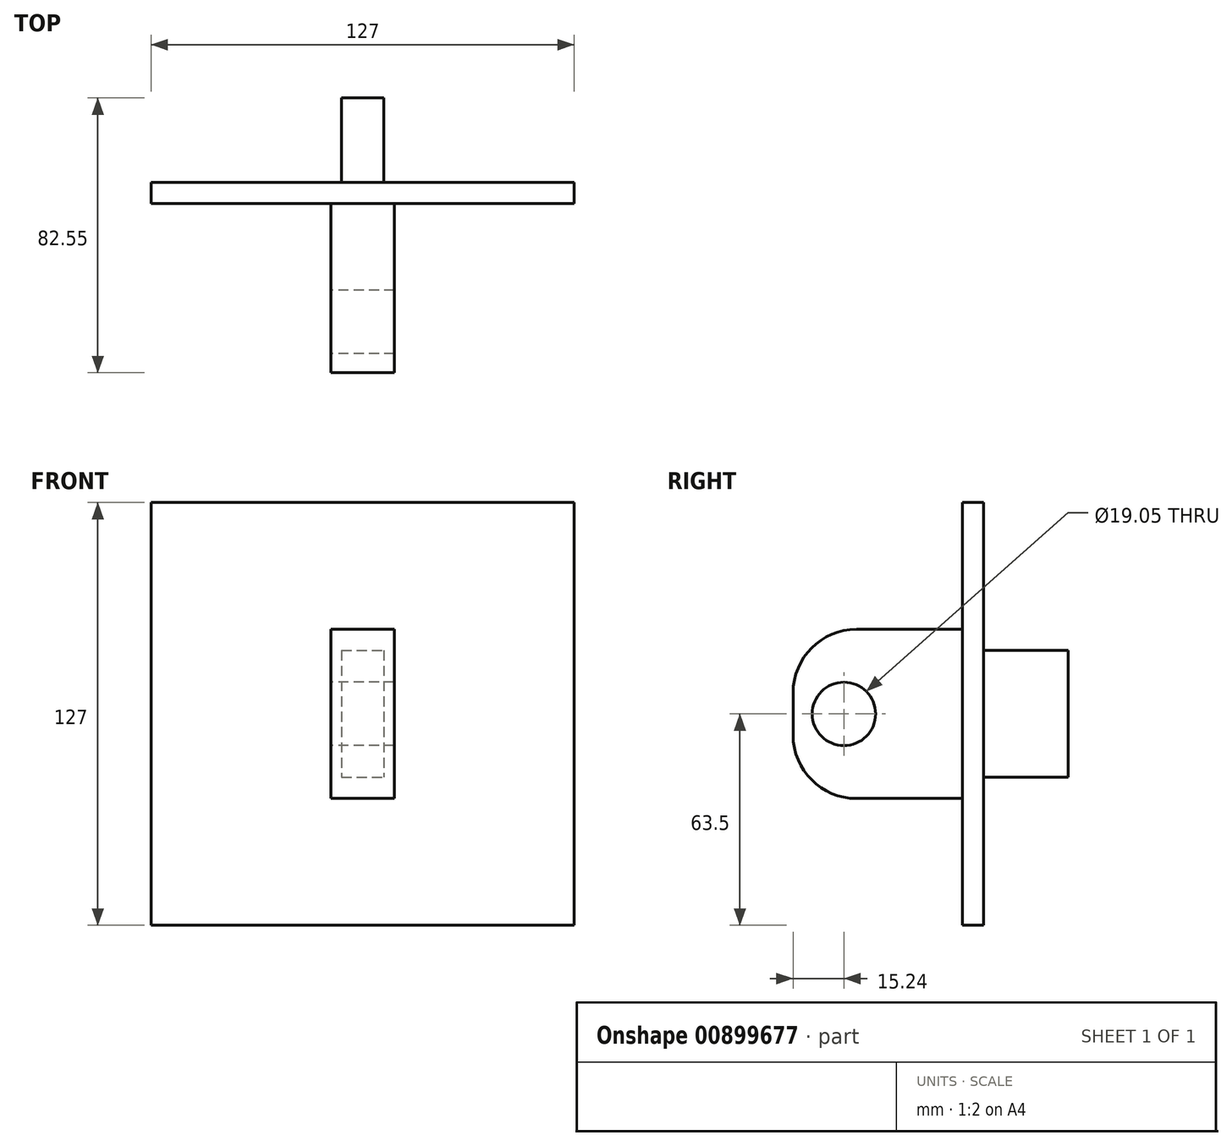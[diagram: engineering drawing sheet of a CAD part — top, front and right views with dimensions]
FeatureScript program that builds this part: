
annotation { "Feature Type Name" : "Feature", "Feature Type Description" : "" }
export const myFeature = defineFeature(function(context is Context, id is Id, definition is map)
    precondition{}
    {
        {
            var Q0;
            Q0=qCreatedBy(makeId("Front.planeOp"),FACE);
            var sketch = newSketch(context, id + "F0", { "sketchPlane" : qUnion([Q0])});
            skLineSegment(sketch, "E0.bottom", {"start": v(63.5, 63.5) * mm, "end": v(-63.5, 63.5) * mm});
            skLineSegment(sketch, "E0.top", {"start": v(63.5, -63.5) * mm, "end": v(-63.5, -63.5) * mm});
            skLineSegment(sketch, "E0.left", {"start": v(63.5, 63.5) * mm, "end": v(63.5, -63.5) * mm});
            skLineSegment(sketch, "E0.right", {"start": v(-63.5, 63.5) * mm, "end": v(-63.5, -63.5) * mm});
            skPoint(sketch, "E0.middle", {"position": v(0, 0) * mm});
            skSolve(sketch);
        }
        {
            var Q0;
            Q0 = qSketchRegion(id + "F0", true);
            extrude(context, id + "F1", {"entities" : qUnion([Q0]), "depth" : 6.35 * mm, "offsetDistance" : 25.4 * mm});
        }
        {
            var Q0;
            Q0=makeQuery(id+"F1.opExtrude","CAP_FACE",FACE,{"disambiguationData":[OSD([sQuery(id+"F0.wireOp",EDGE,"E0.bottom"),sQuery(id+"F0.wireOp",EDGE,"E0.top"),sQuery(id+"F0.wireOp",EDGE,"E0.left"),sQuery(id+"F0.wireOp",EDGE,"E0.right")])],"isStart":false});
            var sketch = newSketch(context, id + "F2", { "sketchPlane" : qUnion([Q0])});
            skLineSegment(sketch, "E1.bottom", {"start": v(9.53, 25.4) * mm, "end": v(-9.52, 25.4) * mm});
            skLineSegment(sketch, "E1.top", {"start": v(9.53, -25.4) * mm, "end": v(-9.53, -25.4) * mm});
            skLineSegment(sketch, "E1.left", {"start": v(9.53, 25.4) * mm, "end": v(9.53, -25.4) * mm});
            skLineSegment(sketch, "E1.right", {"start": v(-9.52, 25.4) * mm, "end": v(-9.53, -25.4) * mm});
            skPoint(sketch, "E1.middle", {"position": v(0, 0) * mm});
            skSolve(sketch);
        }
        {
            var Q0;
            Q0 = qSketchRegion(id + "F2", true);
            extrude(context, id + "F3", {"entities" : qUnion([Q0]), "operationType" : NewBodyOperationType.ADD, "depth" : 50.8 * mm, "offsetDistance" : 25.4 * mm});
        }
        {
            var Q0;
            Q0=makeQuery(id+"F3.opExtrude","SWEPT_FACE",FACE,{"disambiguationData":[OSD([sQuery(id+"F2.wireOp",EDGE,"E1.right")])]});
            var sketch = newSketch(context, id + "F4", { "sketchPlane" : qUnion([Q0])});
            skCircle(sketch, "E2", {"center": v(41.91, 0) * mm, "radius": 9.53 * mm});
            skPoint(sketch, "E2.centerSnap0", {"position": v(57.15, 0) * mm});
            skSolve(sketch);
        }
        {
            var Q0;
            Q0 = qSketchRegion(id + "F4", true);
            extrude(context, id + "F5", {"entities" : qUnion([Q0]), "operationType" : NewBodyOperationType.REMOVE, "endBound" : BoundingType.THROUGH_ALL, "oppositeDirection" : true, "depth" : 25.4 * mm, "offsetDistance" : 25.4 * mm});
        }
        {
            var Q0;
            Q0=makeQuery(id+"F1.opExtrude","CAP_FACE",FACE,{"disambiguationData":[OSD([sQuery(id+"F0.wireOp",EDGE,"E0.bottom"),sQuery(id+"F0.wireOp",EDGE,"E0.top"),sQuery(id+"F0.wireOp",EDGE,"E0.left"),sQuery(id+"F0.wireOp",EDGE,"E0.right")])],"isStart":true});
            var sketch = newSketch(context, id + "F6", { "sketchPlane" : qUnion([Q0])});
            skLineSegment(sketch, "E3.bottom", {"start": v(6.35, 19.05) * mm, "end": v(-6.35, 19.05) * mm});
            skLineSegment(sketch, "E3.top", {"start": v(6.35, -19.05) * mm, "end": v(-6.35, -19.05) * mm});
            skLineSegment(sketch, "E3.left", {"start": v(6.35, 19.05) * mm, "end": v(6.35, -19.05) * mm});
            skLineSegment(sketch, "E3.right", {"start": v(-6.35, 19.05) * mm, "end": v(-6.35, -19.05) * mm});
            skPoint(sketch, "E3.middle", {"position": v(0, 0) * mm});
            skSolve(sketch);
        }
        {
            var Q0;
            Q0 = qSketchRegion(id + "F6", true);
            extrude(context, id + "F7", {"entities" : qUnion([Q0]), "operationType" : NewBodyOperationType.ADD, "depth" : 25.4 * mm, "offsetDistance" : 25.4 * mm});
        }
        {
            var Q0;
            Q0=makeQuery(id+"F3.opExtrude","CAP_EDGE",EDGE,{"disambiguationData":[OSD([sQuery(id+"F2.wireOp",EDGE,"E1.bottom")])],"isStart":false});
            var Q1;
            Q1=makeQuery(id+"F3.opExtrude","CAP_EDGE",EDGE,{"disambiguationData":[OSD([sQuery(id+"F2.wireOp",EDGE,"E1.top")])],"isStart":false});
            fillet(context, id + "F8", {"entities" : qUnion([Q0, Q1]), "radius" : 19.05 * mm, "tangentPropagation" : true, "allowEdgeOverflow" : false});
        }
    });
